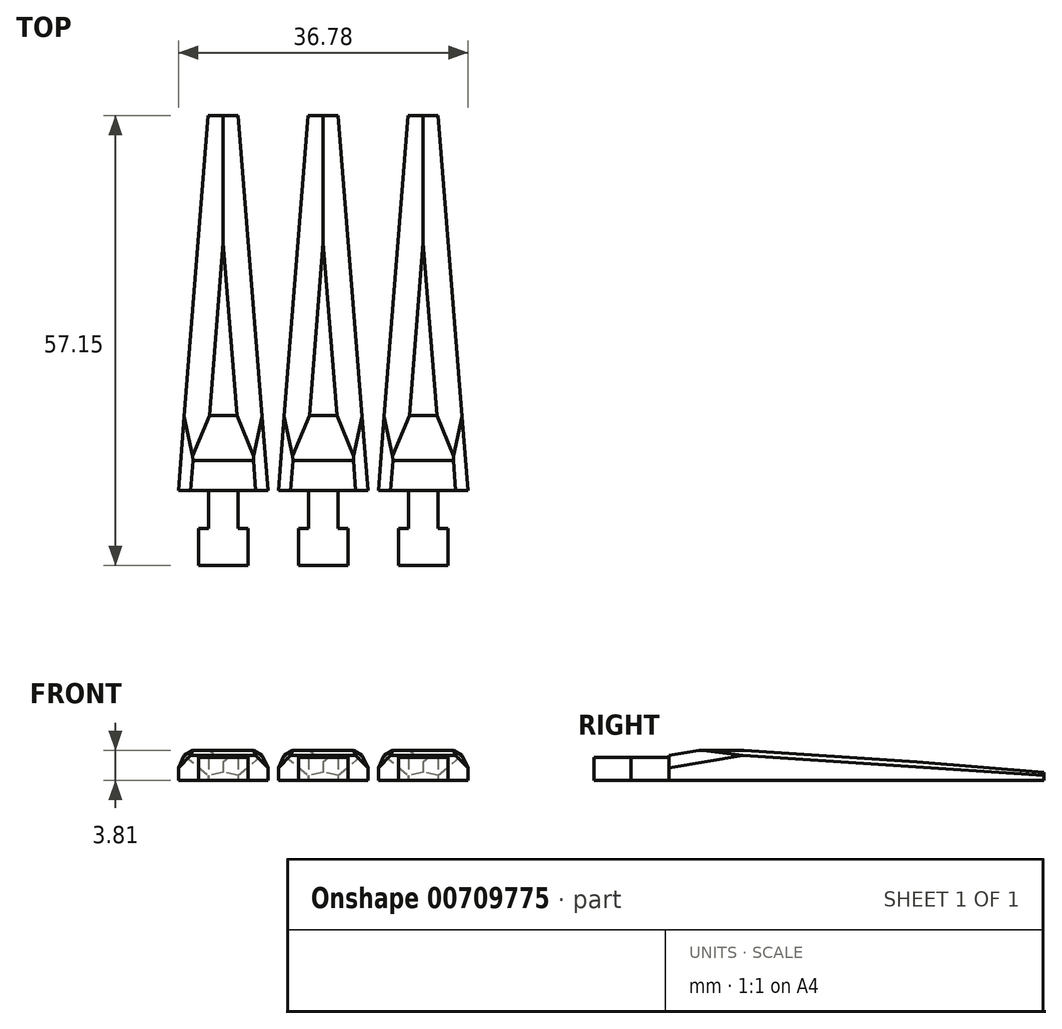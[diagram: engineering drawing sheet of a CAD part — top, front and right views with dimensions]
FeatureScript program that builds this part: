
annotation { "Feature Type Name" : "Feature", "Feature Type Description" : "" }
export const myFeature = defineFeature(function(context is Context, id is Id, definition is map)
    precondition{}
    {
        {
            var Q0;
            Q0=qCreatedBy(makeId("Top.planeOp"),FACE);
            var sketch = newSketch(context, id + "F0", { "sketchPlane" : qUnion([Q0])});
            skLineSegment(sketch, "E0.bottom", {"start": v(3.15, 2.36) * mm, "end": v(-3.15, 2.36) * mm});
            skLineSegment(sketch, "E0.top", {"start": v(3.15, -2.36) * mm, "end": v(-3.15, -2.36) * mm});
            skLineSegment(sketch, "E0.left", {"start": v(3.15, 2.36) * mm, "end": v(3.15, -2.36) * mm});
            skLineSegment(sketch, "E0.right", {"start": v(-3.15, 2.36) * mm, "end": v(-3.15, -2.36) * mm});
            skPoint(sketch, "E0.middle", {"position": v(0, 0) * mm});
            skLineSegment(sketch, "E1", {"start": v(0, 2.36) * mm, "end": v(0, 7.16) * mm});
            skLineSegment(sketch, "E2", {"start": v(0, 7.16) * mm, "end": v(1.88, 7.16) * mm});
            skLineSegment(sketch, "E3", {"start": v(0, 7.16) * mm, "end": v(-1.88, 7.16) * mm});
            skLineSegment(sketch, "E4", {"start": v(-1.88, 7.16) * mm, "end": v(-1.88, 2.36) * mm});
            skLineSegment(sketch, "E5", {"start": v(1.88, 7.16) * mm, "end": v(1.88, 2.36) * mm});
            skLineSegment(sketch, "E6", {"start": v(1.88, 7.16) * mm, "end": v(5.69, 7.16) * mm});
            skLineSegment(sketch, "E7", {"start": v(-1.88, 7.16) * mm, "end": v(-5.69, 7.16) * mm});
            skLineSegment(sketch, "E8", {"start": v(0, 51.61) * mm, "end": v(0, 54.79) * mm});
            skLineSegment(sketch, "E9", {"start": v(0, 54.79) * mm, "end": v(1.9, 54.79) * mm});
            skLineSegment(sketch, "E10", {"start": v(0, 54.79) * mm, "end": v(-1.9, 54.79) * mm});
            skLineSegment(sketch, "E11", {"start": v(-1.9, 54.79) * mm, "end": v(-5.69, 7.16) * mm});
            skLineSegment(sketch, "E12", {"start": v(5.69, 7.16) * mm, "end": v(1.9, 54.79) * mm});
            skSolve(sketch);
        }
        {
            var Q0;
            Q0=makeQuery(id+"F0.imprint","IMPRINT",FACE,{"disambiguationData":[TD([[makeQuery(id+"F0.imprint","IMPRINT",EDGE,{"derivedFrom":sQuery(id+"F0.wireOp",EDGE,"E0.top")}),-1.0]])]});
            var Q1;
            {var subQ0=sQuery(id+"F0.wireOp",EDGE,"E1");Q1=makeQuery(id+"F0.imprint","IMPRINT",FACE,{"disambiguationData":[TD([[makeQuery(id+"F0.imprint","IMPRINT",EDGE,{"derivedFrom":subQ0}),-1.0]])]});}
            var Q2;
            {var subQ0=sQuery(id+"F0.wireOp",EDGE,"E1");Q2=makeQuery(id+"F0.imprint","IMPRINT",FACE,{"disambiguationData":[TD([[makeQuery(id+"F0.imprint","IMPRINT",EDGE,{"derivedFrom":subQ0}),1.0]])]});}
            extrude(context, id + "F1", {"entities" : qUnion([Q0, Q1, Q2]), "depth" : 2.92 * mm, "offsetDistance" : 25.4 * mm});
        }
        {
            var Q0;
            Q0=makeQuery(id+"F0.imprint","IMPRINT",FACE,{"disambiguationData":[TD([[makeQuery(id+"F0.imprint","IMPRINT",EDGE,{"derivedFrom":sQuery(id+"F0.wireOp",EDGE,"E2")}),1.0]])]});
            extrude(context, id + "F2", {"entities" : qUnion([Q0]), "operationType" : NewBodyOperationType.ADD, "depth" : 3.8 * mm, "offsetDistance" : 25.4 * mm});
        }
        {
            var Q0;
            Q0=makeQuery(id+"F2.opExtrude","CAP_EDGE",EDGE,{"disambiguationData":[OSD([sQuery(id+"F0.wireOp",EDGE,"E2"),sQuery(id+"F0.wireOp",EDGE,"E3"),sQuery(id+"F0.wireOp",EDGE,"E6"),sQuery(id+"F0.wireOp",EDGE,"E7")])],"isStart":false});
            chamfer(context, id + "F3", {"entities" : qUnion([Q0]), "chamferType" : ChamferType.TWO_OFFSETS, "width1" : 3.8 * mm, "oppositeDirection" : true, "width2" : 0.64 * mm, "tangentPropagation" : true});
        }
        {
            var Q0;
            Q0=makeQuery(id+"F2.opExtrude","CAP_EDGE",EDGE,{"disambiguationData":[OSD([sQuery(id+"F0.wireOp",EDGE,"E9"),sQuery(id+"F0.wireOp",EDGE,"E10")])],"isStart":false});
            chamfer(context, id + "F4", {"entities" : qUnion([Q0]), "chamferType" : ChamferType.TWO_OFFSETS, "width1" : 38.1 * mm, "oppositeDirection" : true, "width2" : 2.54 * mm, "tangentPropagation" : true});
        }
        {
            var Q0;
            Q0=makeQuery(id+"F3.opChamfer","BLEND_EDGE",EDGE,{"blendedFrom":[makeQuery(id+"F2.opExtrude","CAP_EDGE",EDGE,{"disambiguationData":[OSD([sQuery(id+"F0.wireOp",EDGE,"E2"),sQuery(id+"F0.wireOp",EDGE,"E3"),sQuery(id+"F0.wireOp",EDGE,"E6"),sQuery(id+"F0.wireOp",EDGE,"E7")])],"isStart":false}),makeQuery(id+"F2.opExtrude","SWEPT_FACE",FACE,{"disambiguationData":[OSD([sQuery(id+"F0.wireOp",EDGE,"E12")])]})],"blendedInto":[makeQuery(id+"F2.opExtrude","SWEPT_FACE",FACE,{"disambiguationData":[OSD([sQuery(id+"F0.wireOp",EDGE,"E12")])]})]});
            var Q1;
            Q1=makeQuery(id+"F3.opChamfer","BLEND_EDGE",EDGE,{"blendedFrom":[makeQuery(id+"F2.opExtrude","CAP_EDGE",EDGE,{"disambiguationData":[OSD([sQuery(id+"F0.wireOp",EDGE,"E2"),sQuery(id+"F0.wireOp",EDGE,"E3"),sQuery(id+"F0.wireOp",EDGE,"E6"),sQuery(id+"F0.wireOp",EDGE,"E7")])],"isStart":false}),makeQuery(id+"F2.opExtrude","SWEPT_FACE",FACE,{"disambiguationData":[OSD([sQuery(id+"F0.wireOp",EDGE,"E11")])]})],"blendedInto":[makeQuery(id+"F2.opExtrude","SWEPT_FACE",FACE,{"disambiguationData":[OSD([sQuery(id+"F0.wireOp",EDGE,"E11")])]})]});
            chamfer(context, id + "F5", {"entities" : qUnion([Q0, Q1]), "width" : 1.52 * mm, "tangentPropagation" : true});
        }
        {
            var Q0;
            Q0=makeQuery(id+"F4.opChamfer","BLEND_EDGE",EDGE,{"blendedFrom":[makeQuery(id+"F2.opExtrude","CAP_EDGE",EDGE,{"disambiguationData":[OSD([sQuery(id+"F0.wireOp",EDGE,"E9"),sQuery(id+"F0.wireOp",EDGE,"E10")])],"isStart":false}),makeQuery(id+"F2.opExtrude","SWEPT_FACE",FACE,{"disambiguationData":[OSD([sQuery(id+"F0.wireOp",EDGE,"E11")])]})],"blendedInto":[makeQuery(id+"F2.opExtrude","SWEPT_FACE",FACE,{"disambiguationData":[OSD([sQuery(id+"F0.wireOp",EDGE,"E11")])]})]});
            var Q1;
            Q1=makeQuery(id+"F4.opChamfer","BLEND_EDGE",EDGE,{"blendedFrom":[makeQuery(id+"F2.opExtrude","CAP_EDGE",EDGE,{"disambiguationData":[OSD([sQuery(id+"F0.wireOp",EDGE,"E9"),sQuery(id+"F0.wireOp",EDGE,"E10")])],"isStart":false}),makeQuery(id+"F2.opExtrude","SWEPT_FACE",FACE,{"disambiguationData":[OSD([sQuery(id+"F0.wireOp",EDGE,"E12")])]})],"blendedInto":[makeQuery(id+"F2.opExtrude","SWEPT_FACE",FACE,{"disambiguationData":[OSD([sQuery(id+"F0.wireOp",EDGE,"E12")])]})]});
            chamfer(context, id + "F6", {"entities" : qUnion([Q0, Q1]), "chamferType" : ChamferType.TWO_OFFSETS, "width1" : 0.64 * mm, "oppositeDirection" : false, "width2" : 3.17 * mm, "tangentPropagation" : true});
        }
        {
            var Q0;
            Q0=makeQuery(id+"F1.opExtrude","SWEPT_BODY",BODY,{"disambiguationData":[OSD([sQuery(id+"F0.wireOp",EDGE,"E0.bottom"),sQuery(id+"F0.wireOp",EDGE,"E0.top"),sQuery(id+"F0.wireOp",EDGE,"E0.left"),sQuery(id+"F0.wireOp",EDGE,"E0.right"),sQuery(id+"F0.wireOp",EDGE,"E2"),sQuery(id+"F0.wireOp",EDGE,"E3"),sQuery(id+"F0.wireOp",EDGE,"E4"),sQuery(id+"F0.wireOp",EDGE,"E5")])]});
            transform(context, id + "F7", {"entities" : qUnion([Q0]), "transformType" : TransformType.TRANSLATION_3D, "dx" : 12.7 * mm, "dy" : 0 * mm, "dz" : 0 * mm, "makeCopy" : true});
        }
        {
            var Q0;
            Q0=makeQuery(id+"F1.opExtrude","SWEPT_BODY",BODY,{"disambiguationData":[OSD([sQuery(id+"F0.wireOp",EDGE,"E0.bottom"),sQuery(id+"F0.wireOp",EDGE,"E0.top"),sQuery(id+"F0.wireOp",EDGE,"E0.left"),sQuery(id+"F0.wireOp",EDGE,"E0.right"),sQuery(id+"F0.wireOp",EDGE,"E2"),sQuery(id+"F0.wireOp",EDGE,"E3"),sQuery(id+"F0.wireOp",EDGE,"E4"),sQuery(id+"F0.wireOp",EDGE,"E5")])]});
            transform(context, id + "F8", {"entities" : qUnion([Q0]), "transformType" : TransformType.TRANSLATION_3D, "dx" : -12.7 * mm, "dy" : 0 * mm, "dz" : 0 * mm, "makeCopy" : true});
        }
    });
